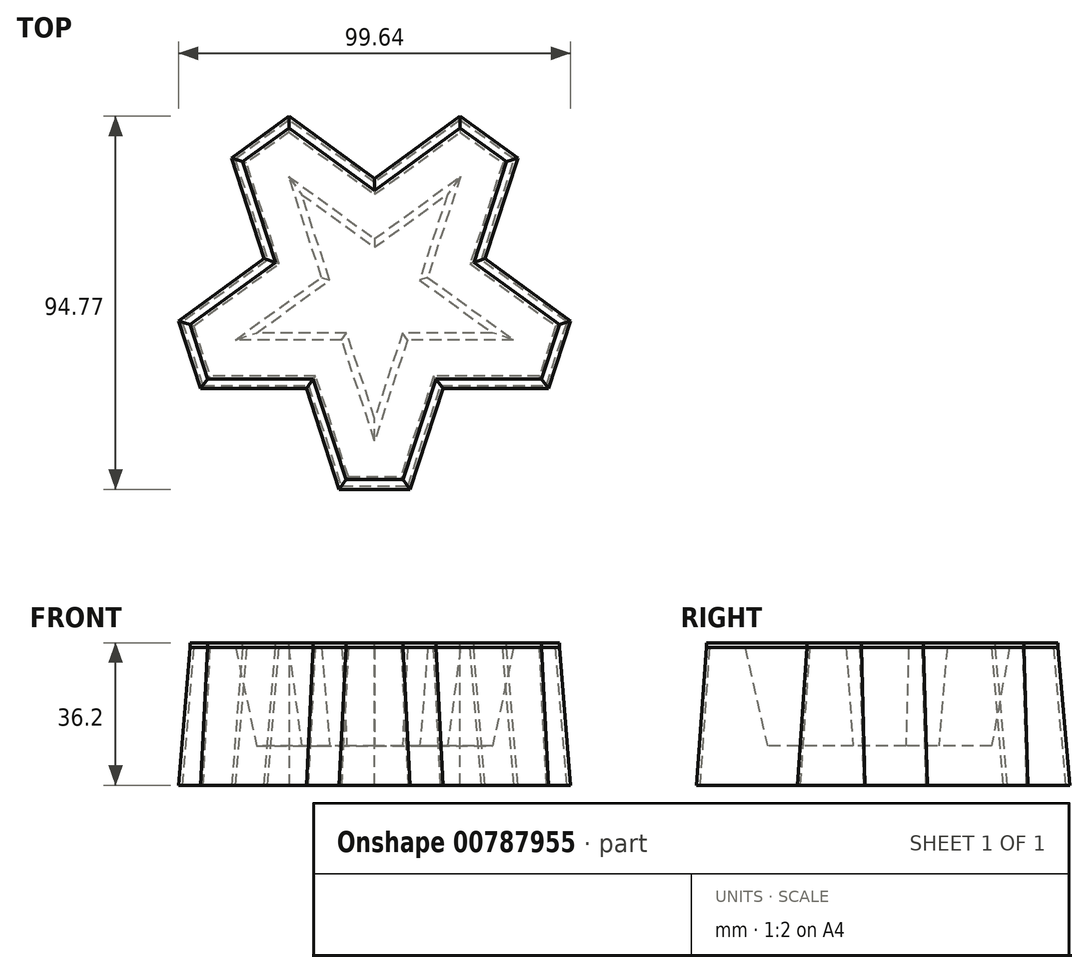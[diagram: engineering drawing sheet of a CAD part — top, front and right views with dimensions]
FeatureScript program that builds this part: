
annotation { "Feature Type Name" : "Feature", "Feature Type Description" : "" }
export const myFeature = defineFeature(function(context is Context, id is Id, definition is map)
    precondition{}
    {
        {
            var Q0;
            Q0=qCreatedBy(makeId("Top.planeOp"),FACE);
            var sketch = newSketch(context, id + "F0", { "sketchPlane" : qUnion([Q0])});
            skCircle(sketch, "E0.cCircle", {"center": v(0, 0) * mm, "radius": 31.5 * mm, "construction": true});
            skLineSegment(sketch, "E0.0", {"start": v(18.52, 25.48) * mm, "end": v(29.96, -9.73) * mm, "construction": true});
            skLineSegment(sketch, "E0.1", {"start": v(29.96, -9.73) * mm, "end": v(0, -31.5) * mm, "construction": true});
            skLineSegment(sketch, "E0.2", {"start": v(0, -31.5) * mm, "end": v(-29.96, -9.73) * mm, "construction": true});
            skLineSegment(sketch, "E0.3", {"start": v(-29.96, -9.73) * mm, "end": v(-18.52, 25.48) * mm, "construction": true});
            skLineSegment(sketch, "E0.4", {"start": v(-18.52, 25.48) * mm, "end": v(18.52, 25.48) * mm, "construction": true});
            skLineSegment(sketch, "E1", {"start": v(-18.52, 25.48) * mm, "end": v(-11.44, 3.72) * mm});
            skLineSegment(sketch, "E2", {"start": v(0, -31.5) * mm, "end": v(7.07, -9.73) * mm});
            skLineSegment(sketch, "E3", {"start": v(18.52, 25.48) * mm, "end": v(0, 12.03) * mm});
            skLineSegment(sketch, "E4", {"start": v(-29.96, -9.73) * mm, "end": v(-7.07, -9.73) * mm});
            skLineSegment(sketch, "E5", {"start": v(29.96, -9.73) * mm, "end": v(11.44, 3.72) * mm});
            skLineSegment(sketch, "E6.trimOffspring", {"start": v(-11.44, 3.72) * mm, "end": v(-29.96, -9.73) * mm});
            skLineSegment(sketch, "E7.trimOffspring", {"start": v(0, 12.03) * mm, "end": v(-18.52, 25.48) * mm});
            skLineSegment(sketch, "E8.trimOffspring", {"start": v(11.44, 3.72) * mm, "end": v(18.52, 25.48) * mm});
            skLineSegment(sketch, "E9.trimOffspring", {"start": v(7.07, -9.73) * mm, "end": v(29.96, -9.73) * mm});
            skLineSegment(sketch, "E10.trimOffspring", {"start": v(-7.07, -9.73) * mm, "end": v(0, -31.5) * mm});
            skSolve(sketch);
        }
        {
            var Q0;
            Q0=qCreatedBy(makeId("Top.planeOp"),FACE);
            cPlane(context, id + "F1", {"entities" : qUnion([Q0]), "cplaneType" : CPlaneType.OFFSET, "offset" : 25 * mm, "width" : 150 * mm, "height" : 150 * mm});
        }
        {
            var Q0;
            Q0=qCreatedBy(id+"F1.planeOp",FACE);
            var sketch = newSketch(context, id + "F2", { "sketchPlane" : qUnion([Q0])});
            skCircle(sketch, "E11.cCircle", {"center": v(0, 0) * mm, "radius": 37 * mm, "construction": true});
            skLineSegment(sketch, "E11.0", {"start": v(21.75, 29.93) * mm, "end": v(35.19, -11.43) * mm, "construction": true});
            skLineSegment(sketch, "E11.1", {"start": v(35.19, -11.43) * mm, "end": v(0, -37) * mm, "construction": true});
            skLineSegment(sketch, "E11.2", {"start": v(0, -37) * mm, "end": v(-35.19, -11.43) * mm, "construction": true});
            skLineSegment(sketch, "E11.3", {"start": v(-35.19, -11.43) * mm, "end": v(-21.75, 29.93) * mm, "construction": true});
            skLineSegment(sketch, "E11.4", {"start": v(-21.75, 29.93) * mm, "end": v(21.75, 29.93) * mm, "construction": true});
            skLineSegment(sketch, "E12", {"start": v(21.75, 29.93) * mm, "end": v(13.44, 4.37) * mm});
            skLineSegment(sketch, "E13", {"start": v(0, -37) * mm, "end": v(-8.3, -11.43) * mm});
            skLineSegment(sketch, "E14", {"start": v(-35.19, -11.43) * mm, "end": v(-13.44, 4.37) * mm});
            skLineSegment(sketch, "E15", {"start": v(-21.75, 29.93) * mm, "end": v(0, 14.13) * mm});
            skLineSegment(sketch, "E16", {"start": v(35.19, -11.43) * mm, "end": v(8.3, -11.43) * mm});
            skLineSegment(sketch, "E17.trimOffspring", {"start": v(0, 14.13) * mm, "end": v(21.75, 29.93) * mm});
            skLineSegment(sketch, "E18.trimOffspring", {"start": v(13.44, 4.37) * mm, "end": v(35.19, -11.43) * mm});
            skLineSegment(sketch, "E19.trimOffspring", {"start": v(8.3, -11.43) * mm, "end": v(0, -37) * mm});
            skLineSegment(sketch, "E20.trimOffspring", {"start": v(-8.3, -11.43) * mm, "end": v(-35.19, -11.43) * mm});
            skLineSegment(sketch, "E21.trimOffspring", {"start": v(-13.44, 4.37) * mm, "end": v(-21.75, 29.93) * mm});
            skSolve(sketch);
        }
        {
            var Q0;
            Q0=qCreatedBy(id+"F1.planeOp",FACE);
            var sketch = newSketch(context, id + "F3", { "sketchPlane" : qUnion([Q0])});
            skLineSegment(sketch, "E22.0", {"start": v(-21.75, 42.3) * mm, "end": v(0, 26.5) * mm});
            skLineSegment(sketch, "E22.1", {"start": v(-25.2, 8.19) * mm, "end": v(-33.5, 33.75) * mm});
            skLineSegment(sketch, "E22.2", {"start": v(0, 26.5) * mm, "end": v(21.75, 42.3) * mm});
            skLineSegment(sketch, "E22.3", {"start": v(-46.94, -7.61) * mm, "end": v(-25.2, 8.19) * mm});
            skLineSegment(sketch, "E22.4", {"start": v(-15.57, -21.43) * mm, "end": v(-42.45, -21.43) * mm});
            skLineSegment(sketch, "E22.5", {"start": v(-7.27, -47) * mm, "end": v(-15.57, -21.43) * mm});
            skLineSegment(sketch, "E22.6", {"start": v(33.5, 33.75) * mm, "end": v(25.2, 8.19) * mm});
            skLineSegment(sketch, "E22.7", {"start": v(25.2, 8.19) * mm, "end": v(46.94, -7.61) * mm});
            skLineSegment(sketch, "E22.8", {"start": v(42.45, -21.43) * mm, "end": v(15.57, -21.43) * mm});
            skLineSegment(sketch, "E22.9", {"start": v(15.57, -21.43) * mm, "end": v(7.27, -47) * mm});
            skLineSegment(sketch, "E23", {"start": v(21.75, 42.3) * mm, "end": v(33.5, 33.75) * mm});
            skLineSegment(sketch, "E24", {"start": v(46.94, -7.61) * mm, "end": v(42.45, -21.43) * mm});
            skLineSegment(sketch, "E25", {"start": v(-21.75, 42.3) * mm, "end": v(-33.5, 33.75) * mm});
            skLineSegment(sketch, "E26", {"start": v(-46.94, -7.61) * mm, "end": v(-42.45, -21.43) * mm});
            skLineSegment(sketch, "E27", {"start": v(-7.27, -47) * mm, "end": v(7.27, -47) * mm});
            skSolve(sketch);
        }
        {
            var Q0;
            Q0 = qSketchRegion(id + "F3", true);
            extrude(context, id + "F4", {"entities" : qUnion([Q0]), "oppositeDirection" : true, "depth" : 35 * mm, "offsetDistance" : 25 * mm, "hasDraft" : true, "draftAngle" : 4 * degree, "hasSecondDirection" : true, "secondDirectionOppositeDirection" : false, "secondDirectionDepth" : 0.8 * mm});
        }
        {
            var Q0;
            Q0=makeQuery(id+"F4.opExtrude","CAP_FACE",FACE,{"disambiguationData":[OSD([sQuery(id+"F3.wireOp",EDGE,"E22.0"),sQuery(id+"F3.wireOp",EDGE,"E22.1"),sQuery(id+"F3.wireOp",EDGE,"E22.2"),sQuery(id+"F3.wireOp",EDGE,"E22.3"),sQuery(id+"F3.wireOp",EDGE,"E22.4"),sQuery(id+"F3.wireOp",EDGE,"E22.5"),sQuery(id+"F3.wireOp",EDGE,"E22.6"),sQuery(id+"F3.wireOp",EDGE,"E22.7"),sQuery(id+"F3.wireOp",EDGE,"E22.8"),sQuery(id+"F3.wireOp",EDGE,"E22.9"),sQuery(id+"F3.wireOp",EDGE,"E23"),sQuery(id+"F3.wireOp",EDGE,"E24"),sQuery(id+"F3.wireOp",EDGE,"E25"),sQuery(id+"F3.wireOp",EDGE,"E26"),sQuery(id+"F3.wireOp",EDGE,"E27")])],"isStart":false});
            shell(context, id + "F5", {"entities" : qUnion([Q0]), "thickness" : 0.8 * mm});
        }
        {
            var Q0;
            Q0=makeQuery(id+"F0.imprint","IMPRINT",FACE,{"disambiguationData":[TD([[makeQuery(id+"F0.imprint","IMPRINT",EDGE,{"derivedFrom":sQuery(id+"F0.wireOp",EDGE,"E1")}),1.0]])]});
            extrude(context, id + "F6", {"entities" : qUnion([Q0]), "operationType" : NewBodyOperationType.ADD, "endBound" : BoundingType.UP_TO_NEXT, "depth" : 25 * mm, "offsetDistance" : 25 * mm, "hasDraft" : true, "draftAngle" : 4 * degree});
        }
        {
            var Q0;
            Q0=makeQuery(id+"F4.opExtrude","CAP_FACE",FACE,{"disambiguationData":[OSD([sQuery(id+"F3.wireOp",EDGE,"E22.0"),sQuery(id+"F3.wireOp",EDGE,"E22.1"),sQuery(id+"F3.wireOp",EDGE,"E22.2"),sQuery(id+"F3.wireOp",EDGE,"E22.3"),sQuery(id+"F3.wireOp",EDGE,"E22.4"),sQuery(id+"F3.wireOp",EDGE,"E22.5"),sQuery(id+"F3.wireOp",EDGE,"E22.6"),sQuery(id+"F3.wireOp",EDGE,"E22.7"),sQuery(id+"F3.wireOp",EDGE,"E22.8"),sQuery(id+"F3.wireOp",EDGE,"E22.9"),sQuery(id+"F3.wireOp",EDGE,"E23"),sQuery(id+"F3.wireOp",EDGE,"E24"),sQuery(id+"F3.wireOp",EDGE,"E25"),sQuery(id+"F3.wireOp",EDGE,"E26"),sQuery(id+"F3.wireOp",EDGE,"E27")])],"isStart":true});
            extrude(context, id + "F7", {"entities" : qUnion([Q0]), "operationType" : NewBodyOperationType.ADD, "depth" : 0.4 * mm, "offsetDistance" : 25 * mm});
        }
    });
